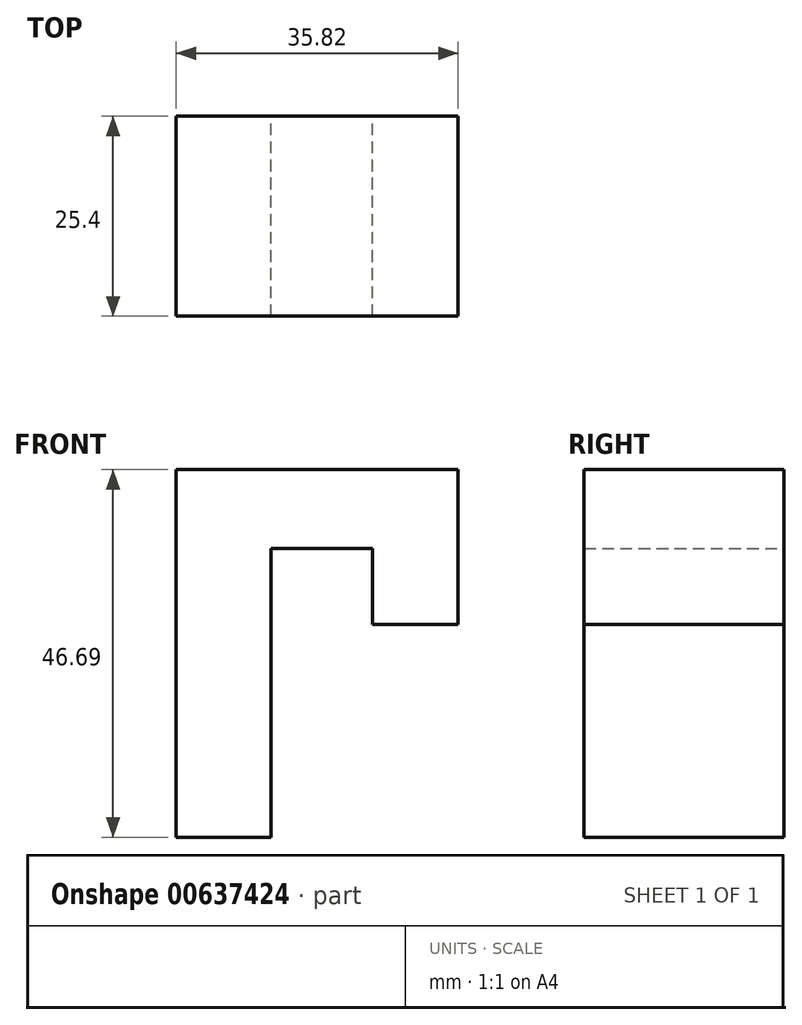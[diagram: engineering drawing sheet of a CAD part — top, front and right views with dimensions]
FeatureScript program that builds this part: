
annotation { "Feature Type Name" : "Feature", "Feature Type Description" : "" }
export const myFeature = defineFeature(function(context is Context, id is Id, definition is map)
    precondition{}
    {
        {
            var Q0;
            Q0=qCreatedBy(makeId("Front.planeOp"),FACE);
            var sketch = newSketch(context, id + "F0", { "sketchPlane" : qUnion([Q0])});
            skLineSegment(sketch, "E0", {"start": v(-58.58, 35.53) * mm, "end": v(-58.58, -11.16) * mm});
            skLineSegment(sketch, "E1", {"start": v(-58.58, -11.16) * mm, "end": v(-46.54, -11.16) * mm});
            skLineSegment(sketch, "E2", {"start": v(-46.54, -11.16) * mm, "end": v(-46.54, 25.54) * mm});
            skLineSegment(sketch, "E3", {"start": v(-46.54, 25.54) * mm, "end": v(-33.62, 25.54) * mm});
            skLineSegment(sketch, "E4", {"start": v(-33.62, 25.54) * mm, "end": v(-33.62, 15.86) * mm});
            skLineSegment(sketch, "E5", {"start": v(-33.62, 15.86) * mm, "end": v(-22.76, 15.86) * mm});
            skLineSegment(sketch, "E6", {"start": v(-22.76, 15.86) * mm, "end": v(-22.76, 35.53) * mm});
            skLineSegment(sketch, "E7", {"start": v(-22.76, 35.53) * mm, "end": v(-58.58, 35.53) * mm});
            skSolve(sketch);
        }
        {
            var Q0;
            Q0 = qSketchRegion(id + "F0", true);
            extrude(context, id + "F1", {"entities" : qUnion([Q0]), "depth" : 25.4 * mm, "offsetDistance" : 25.4 * mm});
        }
    });
